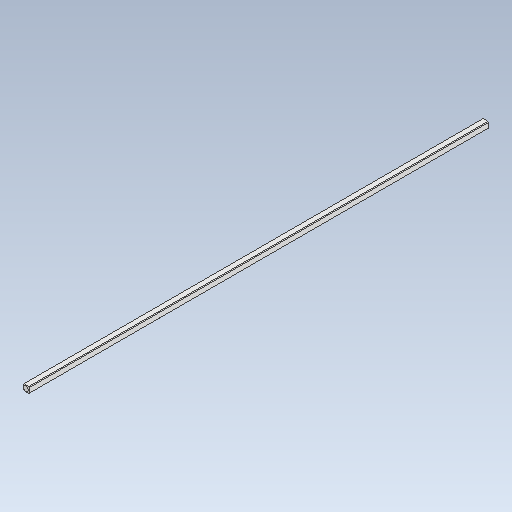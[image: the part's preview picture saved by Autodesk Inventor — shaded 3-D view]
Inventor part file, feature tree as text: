
AUTODESK INVENTOR PART (.ipt)
format: ipt  version: 2021 (Build 250183000, 183)  size: 102,912 bytes
history: mixed  units: in
note: dims shown in document units (in); Inventor stores cm internally (conversion verified against a paired STEP export)
features: mirror x1, imported_body x1
ambient origin geometry x8: Origin, YZ Plane, XZ Plane, XY Plane, X Axis, Y Axis, Z Axis, Center Point
bodies: Solid1 (imported_parasolid)
feature tree (2):
  mirror  "Mirror1"
  imported_body  NMx_Import_Brep_tag  [imported B-rep: ~12 faces, bbox_mm=[3.175, 3.175, 241.3]]
